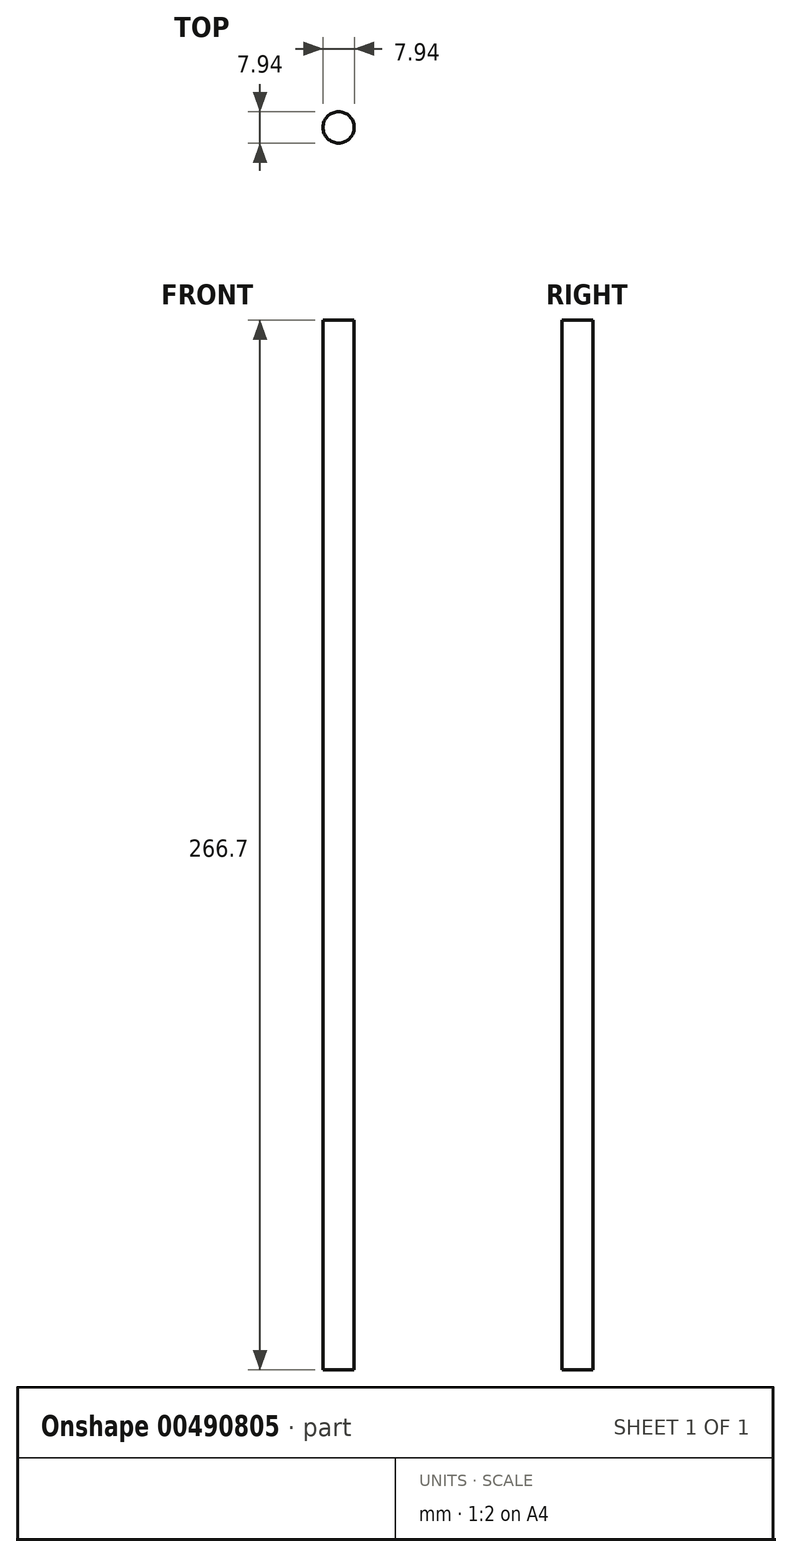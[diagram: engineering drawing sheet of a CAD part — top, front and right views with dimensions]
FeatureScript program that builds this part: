
annotation { "Feature Type Name" : "Feature", "Feature Type Description" : "" }
export const myFeature = defineFeature(function(context is Context, id is Id, definition is map)
    precondition{}
    {
        {
            var Q0;
            Q0=qCreatedBy(makeId("Top.planeOp"),FACE);
            var sketch = newSketch(context, id + "F0", { "sketchPlane" : qUnion([Q0])});
            skCircle(sketch, "E0", {"center": v(-34.47, -43.18) * mm, "radius": 3.97 * mm});
            skSolve(sketch);
        }
        {
            var Q0;
            Q0=qSketchRegion(id+"F0",true);
            extrude(context, id + "F1", {"entities" : qUnion([Q0]), "depth" : 266.7 * mm});
        }
    });
